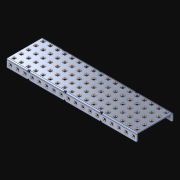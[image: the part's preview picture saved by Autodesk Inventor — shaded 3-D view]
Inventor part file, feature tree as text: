
AUTODESK INVENTOR PART (.ipt)
format: ipt  version: 2021 (Build 250183000, 183)  size: 1,893,888 bytes
history: native  units: in
note: dims shown in document units (in); Inventor stores cm internally (conversion verified against a paired STEP export)
features: extrude x127, other x127, sketch x4, pattern_linear x3
ambient origin geometry x8: Origin, YZ Plane, XZ Plane, XY Plane, X Axis, Y Axis, Z Axis, Center Point
bodies: Solid1 (feature_tree)
feature tree (261):
  pattern_linear  "Rectangular Pattern1"  Spacing1=0.182in  [1 undecoded]
  pattern_linear  "Rectangular Pattern2"  Spacing1=0.046in  [1 undecoded]
  pattern_linear  "Rectangular Pattern3"  Spacing1=0.5in  [1 undecoded]
  extrude  "Extrusion1"  Depth=0.046in
  sketch  "Sketch1"  dims[d0=0.182in]
  other  "Srf1"
  sketch  "Sketch2"  dims[d1=0.046in d2=0.0in]
  other  "Srf2"
  sketch  "Sketch3"  dims[d3=0.182in]
  other  "Srf3"
  other  "Srf4"
  other  "Srf5"
  other  "Srf6"
  other  "Srf7"
  other  "Srf8"
  other  "Srf9"
  other  "Srf10"
  other  "Srf11"
  other  "Srf12"
  other  "Srf13"
  other  "Srf14"
  other  "Srf15"
  other  "Srf16"
  other  "Srf17"
  other  "Srf18"
  other  "Srf19"
  other  "Srf20"
  other  "Srf38"
  other  "Srf39"
  other  "Srf40"
  other  "Srf41"
  other  "Srf42"
  other  "Srf43"
  other  "Srf44"
  other  "Srf45"
  other  "Srf46"
  other  "Srf47"
  other  "Srf48"
  other  "Srf49"
  other  "Srf50"
  other  "Srf51"
  other  "Srf52"
  other  "Srf53"
  other  "Srf54"
  other  "Srf72"
  other  "Srf73"
  other  "Srf74"
  other  "Srf75"
  other  "Srf76"
  other  "Srf77"
  other  "Srf78"
  other  "Srf79"
  other  "Srf80"
  other  "Srf81"
  other  "Srf82"
  other  "Srf83"
  other  "Srf84"
  other  "Srf85"
  other  "Srf86"
  other  "Srf87"
  other  "Srf88"
  other  "Srf89"
  other  "Srf107"
  other  "Srf108"
  other  "Srf109"
  other  "Srf110"
  other  "Srf111"
  other  "Srf112"
  other  "Srf113"
  other  "Srf114"
  other  "Srf115"
  other  "Srf116"
  other  "Srf117"
  other  "Srf118"
  other  "Srf119"
  other  "Srf120"
  other  "Srf121"
  other  "Srf122"
  other  "Srf123"
  other  "Srf124"
  other  "Srf142"
  other  "Srf143"
  other  "Srf144"
  other  "Srf145"
  other  "Srf146"
  other  "Srf147"
  other  "Srf148"
  other  "Srf149"
  other  "Srf150"
  other  "Srf151"
  other  "Srf152"
  other  "Srf153"
  other  "Srf154"
  other  "Srf155"
  other  "Srf156"
  other  "Srf157"
  other  "Srf158"
  other  "Srf159"
  other  "Srf177"
  other  "Srf178"
  other  "Srf179"
  other  "Srf180"
  other  "Srf181"
  other  "Srf182"
  other  "Srf183"
  other  "Srf184"
  other  "Srf185"
  other  "Srf186"
  other  "Srf187"
  other  "Srf188"
  other  "Srf189"
  other  "Srf190"
  other  "Srf191"
  other  "Srf192"
  other  "Srf193"
  other  "Srf194"
  other  "Srf212"
  other  "Srf213"
  other  "Srf214"
  other  "Srf215"
  other  "Srf216"
  other  "Srf217"
  other  "Srf218"
  other  "Srf219"
  other  "Srf220"
  other  "Srf221"
  other  "Srf222"
  other  "Srf223"
  other  "Srf224"
  other  "Srf225"
  other  "Srf226"
  other  "Srf227"
  other  "Srf228"
  sketch  "Sketch4"  dims[d4=0.046in d5=0.0in d6=0.182in d7=0.046in d8=0.0in d11=0.5in d12=7.0866in d14=0.5in d15=1.9685in d17=0.5in d18=7.0866in d20=0.5in d21=8.5in d22=0.0in]
  parser-record x1  (decoder bookkeeping rows leaked as tree rows — omitted from the tree; the rows remain in map.json)
  extrude  "ExtrusionSrf1"  Depth=0.046in
  extrude  "ExtrusionSrf2"  Depth=0.046in
  extrude  "ExtrusionSrf3"  Depth=0.046in
  extrude  "ExtrusionSrf4"  Depth=0.046in
  extrude  "ExtrusionSrf5"  Depth=0.046in
  extrude  "ExtrusionSrf6"  TaperAngle=0.0deg  [1 undecoded]
  extrude  "ExtrusionSrf7"  [1 undecoded]
  extrude  "ExtrusionSrf8"  [1 undecoded]
  extrude  "ExtrusionSrf9"  [1 undecoded]
  extrude  "ExtrusionSrf10"  [1 undecoded]
  extrude  "ExtrusionSrf11"  [1 undecoded]
  extrude  "ExtrusionSrf12"  [1 undecoded]
  extrude  "ExtrusionSrf13"  [1 undecoded]
  extrude  "ExtrusionSrf14"  [1 undecoded]
  extrude  "ExtrusionSrf15"  [1 undecoded]
  extrude  "ExtrusionSrf16"  [1 undecoded]
  extrude  "ExtrusionSrf17"  [1 undecoded]
  extrude  "ExtrusionSrf18"  [1 undecoded]
  extrude  "ExtrusionSrf19"  [1 undecoded]
  extrude  "ExtrusionSrf20"  [1 undecoded]
  extrude  "ExtrusionSrf38"  [1 undecoded]
  extrude  "ExtrusionSrf39"  [1 undecoded]
  extrude  "ExtrusionSrf40"  [1 undecoded]
  extrude  "ExtrusionSrf41"  [1 undecoded]
  extrude  "ExtrusionSrf42"  [1 undecoded]
  extrude  "ExtrusionSrf43"  [1 undecoded]
  extrude  "ExtrusionSrf44"  [1 undecoded]
  extrude  "ExtrusionSrf45"  [1 undecoded]
  extrude  "ExtrusionSrf46"  [1 undecoded]
  extrude  "ExtrusionSrf47"  [1 undecoded]
  extrude  "ExtrusionSrf48"  [1 undecoded]
  extrude  "ExtrusionSrf49"  [1 undecoded]
  extrude  "ExtrusionSrf50"  [1 undecoded]
  extrude  "ExtrusionSrf51"  [1 undecoded]
  extrude  "ExtrusionSrf52"  [1 undecoded]
  extrude  "ExtrusionSrf53"  [1 undecoded]
  extrude  "ExtrusionSrf54"  [1 undecoded]
  extrude  "ExtrusionSrf72"  [1 undecoded]
  extrude  "ExtrusionSrf73"  [1 undecoded]
  extrude  "ExtrusionSrf74"  [1 undecoded]
  extrude  "ExtrusionSrf75"  [1 undecoded]
  extrude  "ExtrusionSrf76"  [1 undecoded]
  extrude  "ExtrusionSrf77"  [1 undecoded]
  extrude  "ExtrusionSrf78"  [1 undecoded]
  extrude  "ExtrusionSrf79"  [1 undecoded]
  extrude  "ExtrusionSrf80"  [1 undecoded]
  extrude  "ExtrusionSrf81"  [1 undecoded]
  extrude  "ExtrusionSrf82"  [1 undecoded]
  extrude  "ExtrusionSrf83"  [1 undecoded]
  extrude  "ExtrusionSrf84"  [1 undecoded]
  extrude  "ExtrusionSrf85"  [1 undecoded]
  extrude  "ExtrusionSrf86"  [1 undecoded]
  extrude  "ExtrusionSrf87"  [1 undecoded]
  extrude  "ExtrusionSrf88"  [1 undecoded]
  extrude  "ExtrusionSrf89"  [1 undecoded]
  extrude  "ExtrusionSrf107"  [1 undecoded]
  extrude  "ExtrusionSrf108"  [1 undecoded]
  extrude  "ExtrusionSrf109"  [1 undecoded]
  extrude  "ExtrusionSrf110"  [1 undecoded]
  extrude  "ExtrusionSrf111"  [1 undecoded]
  extrude  "ExtrusionSrf112"  [1 undecoded]
  extrude  "ExtrusionSrf113"  [1 undecoded]
  extrude  "ExtrusionSrf114"  [1 undecoded]
  extrude  "ExtrusionSrf115"  [1 undecoded]
  extrude  "ExtrusionSrf116"  [1 undecoded]
  extrude  "ExtrusionSrf117"  [1 undecoded]
  extrude  "ExtrusionSrf118"  [1 undecoded]
  extrude  "ExtrusionSrf119"  [1 undecoded]
  extrude  "ExtrusionSrf120"  [1 undecoded]
  extrude  "ExtrusionSrf121"  [1 undecoded]
  extrude  "ExtrusionSrf122"  [1 undecoded]
  extrude  "ExtrusionSrf123"  [1 undecoded]
  extrude  "ExtrusionSrf124"  [1 undecoded]
  extrude  "ExtrusionSrf142"  [1 undecoded]
  extrude  "ExtrusionSrf143"  [1 undecoded]
  extrude  "ExtrusionSrf144"  [1 undecoded]
  extrude  "ExtrusionSrf145"  [1 undecoded]
  extrude  "ExtrusionSrf146"  [1 undecoded]
  extrude  "ExtrusionSrf147"  [1 undecoded]
  extrude  "ExtrusionSrf148"  [1 undecoded]
  extrude  "ExtrusionSrf149"  [1 undecoded]
  extrude  "ExtrusionSrf150"  [1 undecoded]
  extrude  "ExtrusionSrf151"  [1 undecoded]
  extrude  "ExtrusionSrf152"  [1 undecoded]
  extrude  "ExtrusionSrf153"  [1 undecoded]
  extrude  "ExtrusionSrf154"  [1 undecoded]
  extrude  "ExtrusionSrf155"  [1 undecoded]
  extrude  "ExtrusionSrf156"  [1 undecoded]
  extrude  "ExtrusionSrf157"  [1 undecoded]
  extrude  "ExtrusionSrf158"  [1 undecoded]
  extrude  "ExtrusionSrf159"  [1 undecoded]
  extrude  "ExtrusionSrf177"  [1 undecoded]
  extrude  "ExtrusionSrf178"  [1 undecoded]
  extrude  "ExtrusionSrf179"  [1 undecoded]
  extrude  "ExtrusionSrf180"  [1 undecoded]
  extrude  "ExtrusionSrf181"  [1 undecoded]
  extrude  "ExtrusionSrf182"  [1 undecoded]
  extrude  "ExtrusionSrf183"  [1 undecoded]
  extrude  "ExtrusionSrf184"  [1 undecoded]
  extrude  "ExtrusionSrf185"  [1 undecoded]
  extrude  "ExtrusionSrf186"  [1 undecoded]
  extrude  "ExtrusionSrf187"  [1 undecoded]
  extrude  "ExtrusionSrf188"  [1 undecoded]
  extrude  "ExtrusionSrf189"  [1 undecoded]
  extrude  "ExtrusionSrf190"  [1 undecoded]
  extrude  "ExtrusionSrf191"  [1 undecoded]
  extrude  "ExtrusionSrf192"  [1 undecoded]
  extrude  "ExtrusionSrf193"  [1 undecoded]
  extrude  "ExtrusionSrf194"  [1 undecoded]
  extrude  "ExtrusionSrf212"  [1 undecoded]
  extrude  "ExtrusionSrf213"  [1 undecoded]
  extrude  "ExtrusionSrf214"  [1 undecoded]
  extrude  "ExtrusionSrf215"  [1 undecoded]
  extrude  "ExtrusionSrf216"  [1 undecoded]
  extrude  "ExtrusionSrf217"  [1 undecoded]
  extrude  "ExtrusionSrf218"  [1 undecoded]
  extrude  "ExtrusionSrf219"  [1 undecoded]
  extrude  "ExtrusionSrf220"  [1 undecoded]
  extrude  "ExtrusionSrf221"  [1 undecoded]
  extrude  "ExtrusionSrf222"  [1 undecoded]
  extrude  "ExtrusionSrf223"  [1 undecoded]
  extrude  "ExtrusionSrf224"  [1 undecoded]
  extrude  "ExtrusionSrf225"  [1 undecoded]
  extrude  "ExtrusionSrf226"  [1 undecoded]
  extrude  "ExtrusionSrf227"  [1 undecoded]
  extrude  "ExtrusionSrf228"  [1 undecoded]
note: 124 required parameter values undecoded (feature->parameter linkage not recoverable at this tier; creation-order binding heuristic only, values carry confidence <= 0.55)
